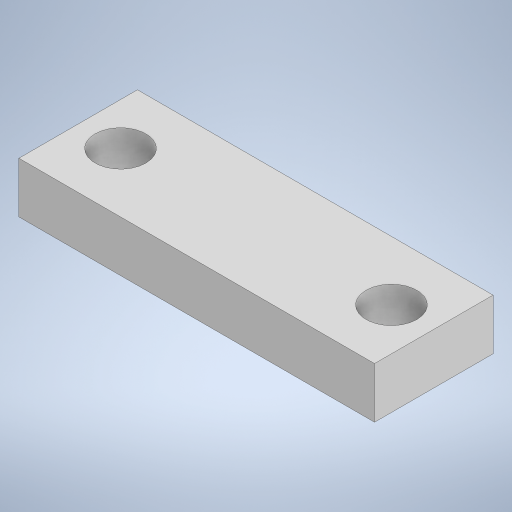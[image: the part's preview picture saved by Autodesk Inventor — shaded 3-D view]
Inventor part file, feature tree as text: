
AUTODESK INVENTOR PART (.ipt)
format: ipt  version: 2023.2 (Build 272271000, 271)  size: 519,680 bytes
history: native  units: mm
features: sketch x1, extrude x1, hole x1
ambient origin geometry x8: Origin, YZ Plane, XZ Plane, XY Plane, X Axis, Y Axis, Z Axis, Center Point
bodies: Solid1 (feature_tree)
feature tree (3):
  sketch  "Sketch1"  dims[d0=42.0mm d1=14.0mm d2=5.0mm d3=5.0mm d4=6.0mm d5=0.0mm d6=6.0mm d7=6.0mm d8=4.0mm d9=2.0mm d10=90.0deg d11=8.0mm d12=20.594885mm]
  extrude  "Extrusion1"  Depth=14.0mm
  hole  "Hole1"  [1 undecoded]
note: 1 required parameter value undecoded (feature->parameter linkage not recoverable at this tier; creation-order binding heuristic only, values carry confidence <= 0.55)
